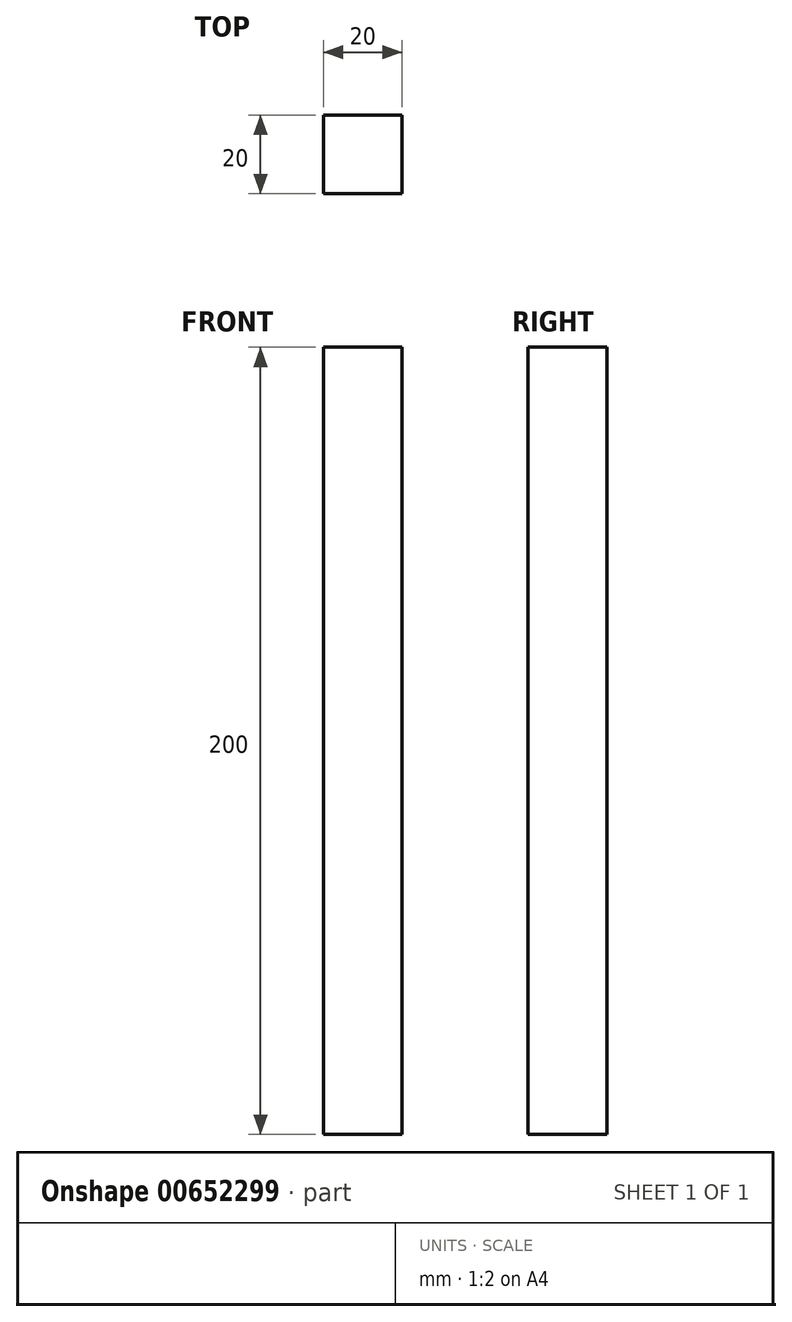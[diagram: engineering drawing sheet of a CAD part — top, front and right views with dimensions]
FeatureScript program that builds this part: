
annotation { "Feature Type Name" : "Feature", "Feature Type Description" : "" }
export const myFeature = defineFeature(function(context is Context, id is Id, definition is map)
    precondition{}
    {
        {
            var Q0;
            Q0=qCreatedBy(makeId("Top.planeOp"),FACE);
            var sketch = newSketch(context, id + "F0", { "sketchPlane" : qUnion([Q0])});
            skLineSegment(sketch, "E0.bottom", {"start": v(0, 0) * mm, "end": v(20, 0) * mm});
            skLineSegment(sketch, "E0.top", {"start": v(0, 20) * mm, "end": v(20, 20) * mm});
            skLineSegment(sketch, "E0.left", {"start": v(0, 0) * mm, "end": v(0, 20) * mm});
            skLineSegment(sketch, "E0.right", {"start": v(20, 0) * mm, "end": v(20, 20) * mm});
            skSolve(sketch);
        }
        {
            var Q0;
            Q0=makeQuery(id+"F0.imprint","IMPRINT",FACE,{"disambiguationData":[TD([[makeQuery(id+"F0.imprint","IMPRINT",EDGE,{"derivedFrom":sQuery(id+"F0.wireOp",EDGE,"E0.bottom")}),1.0]])]});
            extrude(context, id + "F1", {"entities" : qUnion([Q0]), "oppositeDirection" : true, "depth" : 200 * mm, "offsetDistance" : 25 * mm});
        }
    });
